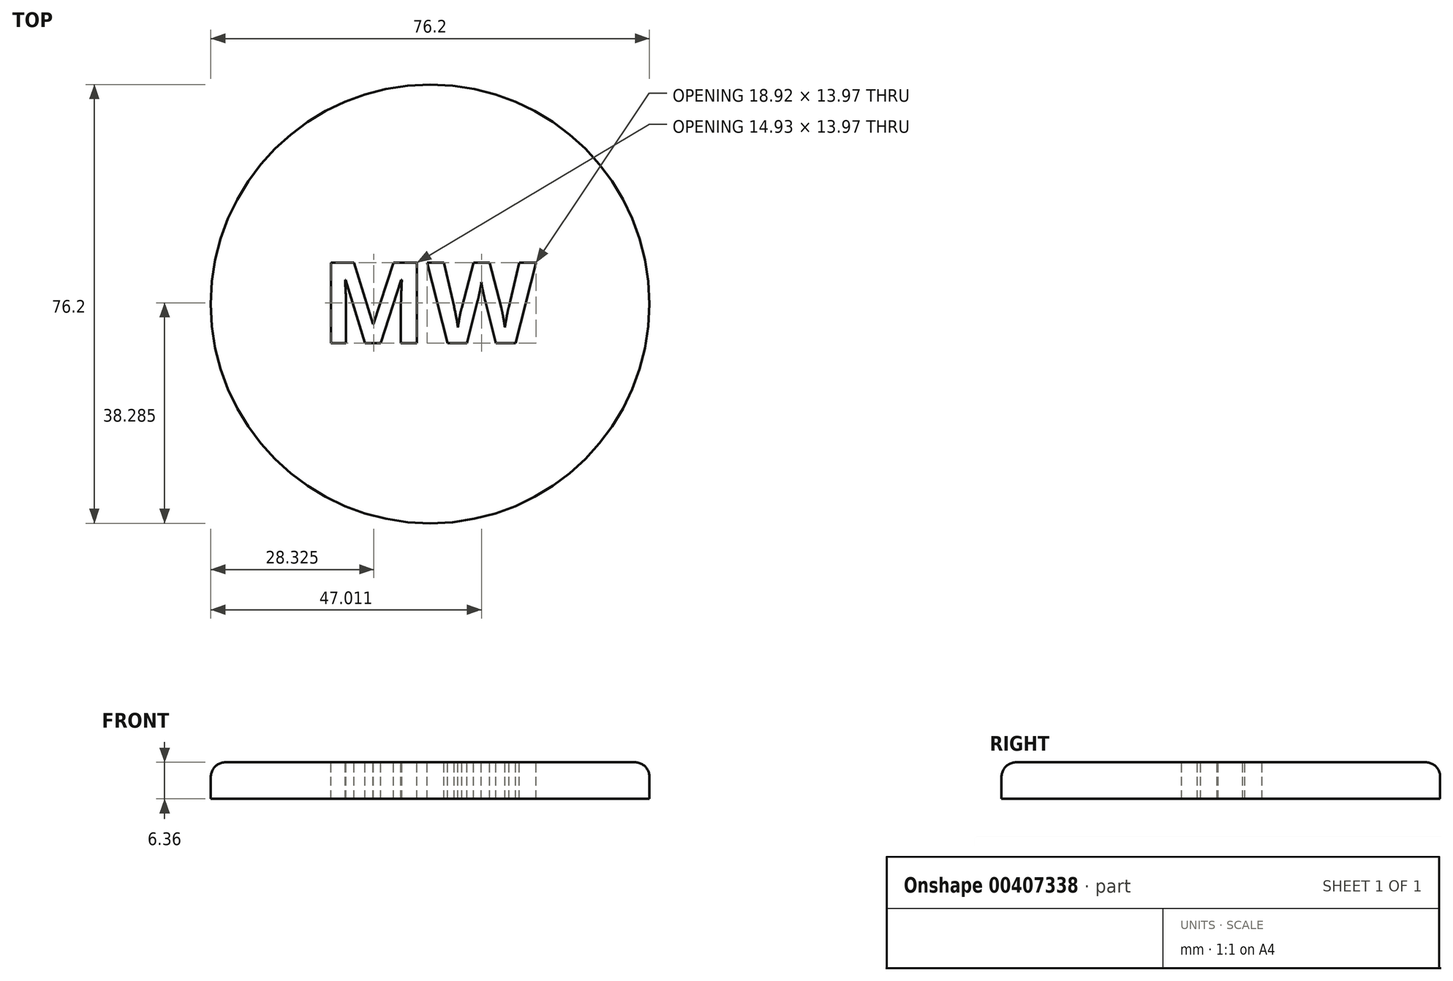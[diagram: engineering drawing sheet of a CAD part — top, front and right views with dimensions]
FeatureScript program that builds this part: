
annotation { "Feature Type Name" : "Feature", "Feature Type Description" : "" }
export const myFeature = defineFeature(function(context is Context, id is Id, definition is map)
    precondition{}
    {
        {
            var Q0;
            Q0=qCreatedBy(makeId("Front.planeOp"),FACE);
            var sketch = newSketch(context, id + "F0", { "sketchPlane" : qUnion([Q0])});
            skLineSegment(sketch, "E0.bottom", {"start": v(38.1, -3.17) * mm, "end": v(-38.1, -3.18) * mm});
            skLineSegment(sketch, "E0.top", {"start": v(38.1, 3.18) * mm, "end": v(-38.1, 3.18) * mm});
            skLineSegment(sketch, "E0.left", {"start": v(38.1, -3.17) * mm, "end": v(38.1, 3.18) * mm});
            skLineSegment(sketch, "E0.right", {"start": v(-38.1, -3.18) * mm, "end": v(-38.1, 3.18) * mm});
            skPoint(sketch, "E0.middle", {"position": v(0, 0) * mm});
            skLineSegment(sketch, "E1", {"start": v(0, 3.18) * mm, "end": v(0, -3.17) * mm});
            skSolve(sketch);
        }
        {
            var Q0;
            {var subQ0=sQuery(id+"F0.wireOp",EDGE,"E0.right");Q0=makeQuery(id+"F0.imprint","IMPRINT",FACE,{"disambiguationData":[TD([[makeQuery(id+"F0.imprint","IMPRINT",EDGE,{"derivedFrom":subQ0}),-1.0]])]});}
            var Q1;
            Q1=sQuery(id+"F0.wireOp",EDGE,"E1");
            revolve(context, id + "F1", {"entities" : qUnion([Q0]), "axis" : qUnion([Q1]), "revolveType" : RevolveType.FULL});
        }
        {
            var Q0;
            Q0=makeQuery(id+"F1.opRevolve","SWEPT_EDGE",EDGE,{"disambiguationData":[OSD([sQuery(id+"F0.wireOp",EDGE,"E0.top"),sQuery(id+"F0.wireOp",EDGE,"E0.right")])]});
            fillet(context, id + "F2", {"entities" : qUnion([Q0]), "radius" : 2.54 * mm, "tangentPropagation" : true, "allowEdgeOverflow" : false});
        }
        {
            var Q0;
            Q0=qCreatedBy(makeId("Top.planeOp"),FACE);
            var sketch = newSketch(context, id + "F3", { "sketchPlane" : qUnion([Q0])});
            skText(sketch, "E2", { "text": "MW", "fontName": "OpenSans-Bold.ttf"});
            const initialGuessF3  = {"E2": [-0.019, -0.0068, 1, 0, 0.01409]};
            skSetInitialGuess(sketch, initialGuessF3);
            skSolve(sketch);
        }
        {
            var Q0;
            Q0 = qSketchRegion(id + "F3", true);
            extrude(context, id + "F4", {"entities" : qUnion([Q0]), "operationType" : NewBodyOperationType.REMOVE, "endBound" : BoundingType.SYMMETRIC, "oppositeDirection" : true, "depth" : 6.6 * mm});
        }
    });
